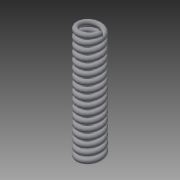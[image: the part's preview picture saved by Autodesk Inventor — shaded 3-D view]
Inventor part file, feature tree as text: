
AUTODESK INVENTOR PART (.ipt)
format: ipt  version: 2014 SP1 (Build 180222100, 222)  size: 495,616 bytes
history: native  units: in
note: dims shown in document units (in); Inventor stores cm internally (conversion verified against a paired STEP export)
features: other x1, helix x1, sketch x1
ambient origin geometry x8: Origin, YZ Plane, XZ Plane, XY Plane, X Axis, Y Axis, Z Axis, Center Point
bodies: Solid1 (feature_tree)
feature tree (3):
  other  "Extractor Spring"
  helix  "Coil1"  [1 undecoded]
  sketch  "Sketch1"  dims[d1=0.1765in d2=0.782in d3=0.748in d4=1.0in d5=0.748in d6=6.2992in d7=0.0in d8=45.0deg d9=45.0deg d10=45.0deg d11=45.0deg]
note: 1 required parameter value undecoded (feature->parameter linkage not recoverable at this tier; creation-order binding heuristic only, values carry confidence <= 0.55)
